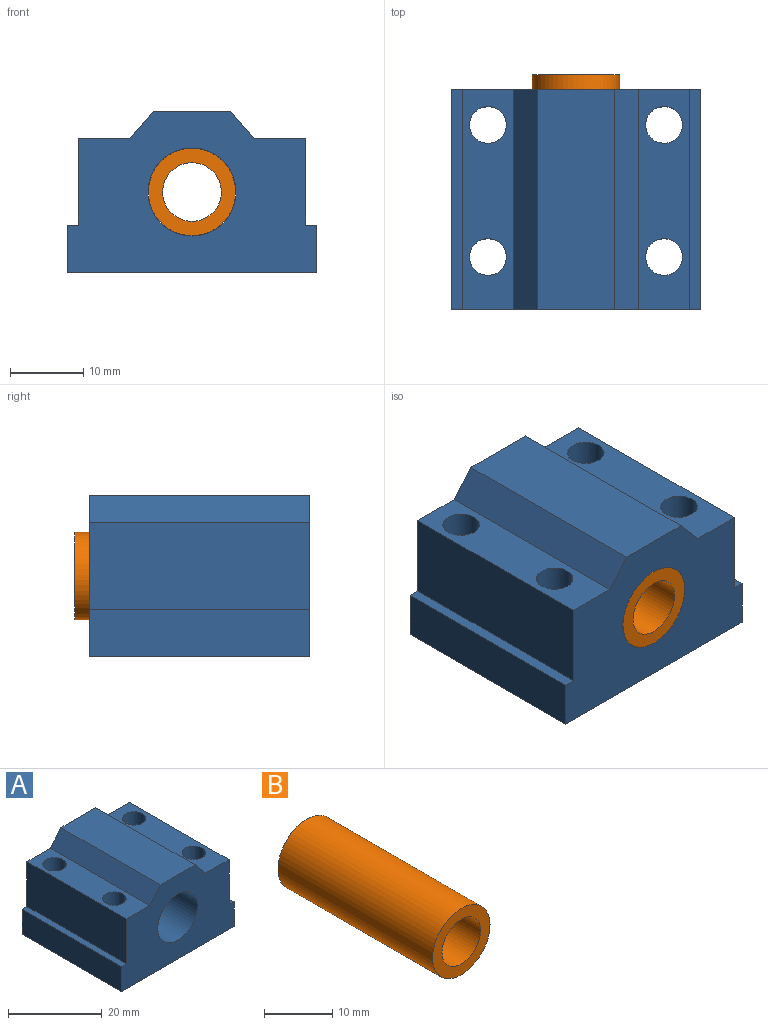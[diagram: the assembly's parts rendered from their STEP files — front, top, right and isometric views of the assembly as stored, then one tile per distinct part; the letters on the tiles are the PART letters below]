
ASSEMBLY  parts=2 mates=1
PART A: 19 faces, bbox 34x30x22 mm
  f0: plane 30x1.5mm, normal (0,0,1), area 45mm2, adj f1,f11,f13,f14
  f1: plane 30x6.5mm, normal (-1,0,0), area 195mm2, adj f0,f2,f13,f14
  f2: plane 34x30mm, normal (0,0,-1), area 941.5mm2, adj f1,f3,f13,f14,f15,f16,f17,f18
  f3: plane 30x6.5mm, normal (1,0,0), area 195mm2, adj f2,f4,f13,f14
  f4: plane 30x1.5mm, normal (0,0,1), area 45mm2, adj f3,f5,f13,f14
  f5: plane 30x11.74mm, normal (1,0,0), area 352.3mm2, adj f4,f6,f13,f14
  f6: plane 30x7mm, normal (0,0,1), area 170.7mm2, adj f5,f7,f13,f14,f17,f18
  f7: plane 30x3.76mm, normal (0.76,0,0.65), area 149mm2, adj f6,f8,f13,f14
  f8: plane 30x10.5mm, normal (0,0,1), area 315mm2, adj f7,f9,f13,f14
  f9: plane 30x3.76mm, normal (-0.76,0,0.65), area 149mm2, adj f8,f10,f13,f14
  f10: plane 30x7mm, normal (0,0,1), area 170.7mm2, adj f9,f11,f13,f14,f15,f16
  f11: plane 30x11.74mm, normal (-1,0,0), area 352.3mm2, adj f0,f10,f13,f14
  f12: cylinder r=6mm len=30mm, axis (0,-1,0), area 1131mm2, adj f13,f14
  f13: plane 34x22mm, normal (0,1,0), area 523.6mm2, adj f0,f1,f2,f3,f4,f5,f6,f7
  f14: plane 34x22mm, normal (0,-1,0), area 523.6mm2, adj f0,f1,f2,f3,f4,f5,f6,f7
  f15: cylinder r=2.5mm len=18.24mm, axis (0,0,-1), area 286.6mm2, adj f2,f10
  f16: cylinder r=2.5mm len=18.24mm, axis (0,0,-1), area 286.6mm2, adj f2,f10
  f17: cylinder r=2.5mm len=18.24mm, axis (0,0,-1), area 286.6mm2, adj f2,f6
  f18: cylinder r=2.5mm len=18.24mm, axis (0,0,-1), area 286.6mm2, adj f2,f6
PART B: 4 faces, bbox 11.9x32x11.9 mm
  f0: cylinder r=4mm len=32mm, axis (0,1,0), area 804.2mm2, adj f2,f3
  f1: cylinder r=5.95mm len=32mm, axis (0,1,0), area 1196.3mm2, adj f2,f3
  f2: plane 11.9x11.9mm, normal (0,-1,0), area 61mm2, adj f0,f1
  f3: plane 11.9x11.9mm, normal (0,1,0), area 61mm2, adj f0,f1
PLACE A at identity
PLACE B t=(-7.7,32,56.27)mm
MATE fastened B.f0 <-> A.f12  axis (0,1,0) through (-7.7,0,56.27)mm
